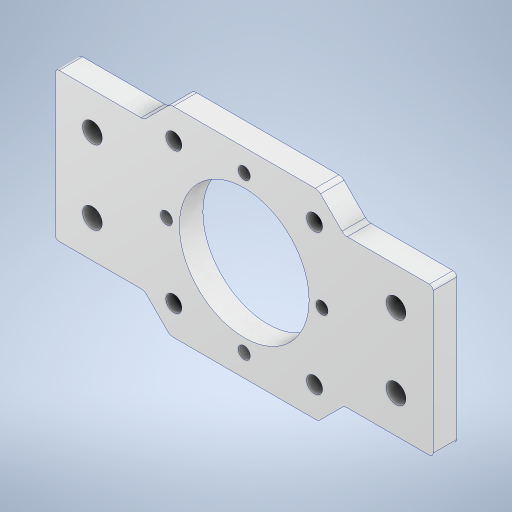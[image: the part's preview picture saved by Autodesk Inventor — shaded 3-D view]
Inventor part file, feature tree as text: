
AUTODESK INVENTOR PART (.ipt)
format: ipt  version: 2024 (Build 280153000, 153)  size: 336,384 bytes
history: native  units: mm
features: sketch x5, hole x3, extrude x2, fillet x2
ambient origin geometry x8: Origin, YZ Plane, XZ Plane, XY Plane, X Axis, Y Axis, Z Axis, Center Point
bodies: Solid1 (feature_tree)
feature tree (12):
  extrude  "Extrusion1"  Depth=40.0mm
  fillet  "Fillet1"  Radius=42.0mm
  fillet  "Fillet2"  Radius=42.0mm
  extrude  "Extrusion2"  Depth=42.0mm
  hole  "Hole1"  [1 undecoded]
  hole  "Hole2"  [1 undecoded]
  hole  "Hole3"  [1 undecoded]
  sketch  "Sketch1"  dims[d0=102.0mm d1=40.0mm d2=42.0mm d3=42.0mm]
  sketch  "Sketch2"  dims[d4=42.0mm d5=42.0mm]
  sketch  "Sketch3"  dims[d6=52.0mm d8=54.0mm]
  sketch  "Sketch4"  dims[d9=6.35mm d10=0.0mm d11=1.0mm]
  sketch  "Sketch5"  dims[d12=2.0mm d13=35.0mm d14=0.0mm d15=0.0mm d17=42.0mm d18=3.242mm d19=8.0mm d20=4.0mm d21=2.0mm d22=90.0deg d23=11.8mm d24=20.594885mm d25=20.0mm d26=10.0mm d27=5.3mm d28=8.0mm d29=4.0mm d30=2.0mm d31=90.0deg d32=8.0mm d33=20.594885mm d34=38.0mm d35=38.0mm d36=4.3mm d37=6.0mm d38=4.0mm d39=2.0mm d40=90.0deg d41=8.0mm d42=20.594885mm d43=7.0mm d44=7.0mm d45=7.0mm d46=7.0mm d47=7.0mm d48=7.0mm d49=7.0mm d50=7.0mm d51=7.0mm d52=6.0mm d53=6.0mm]
note: 3 required parameter values undecoded (feature->parameter linkage not recoverable at this tier; creation-order binding heuristic only, values carry confidence <= 0.55)
